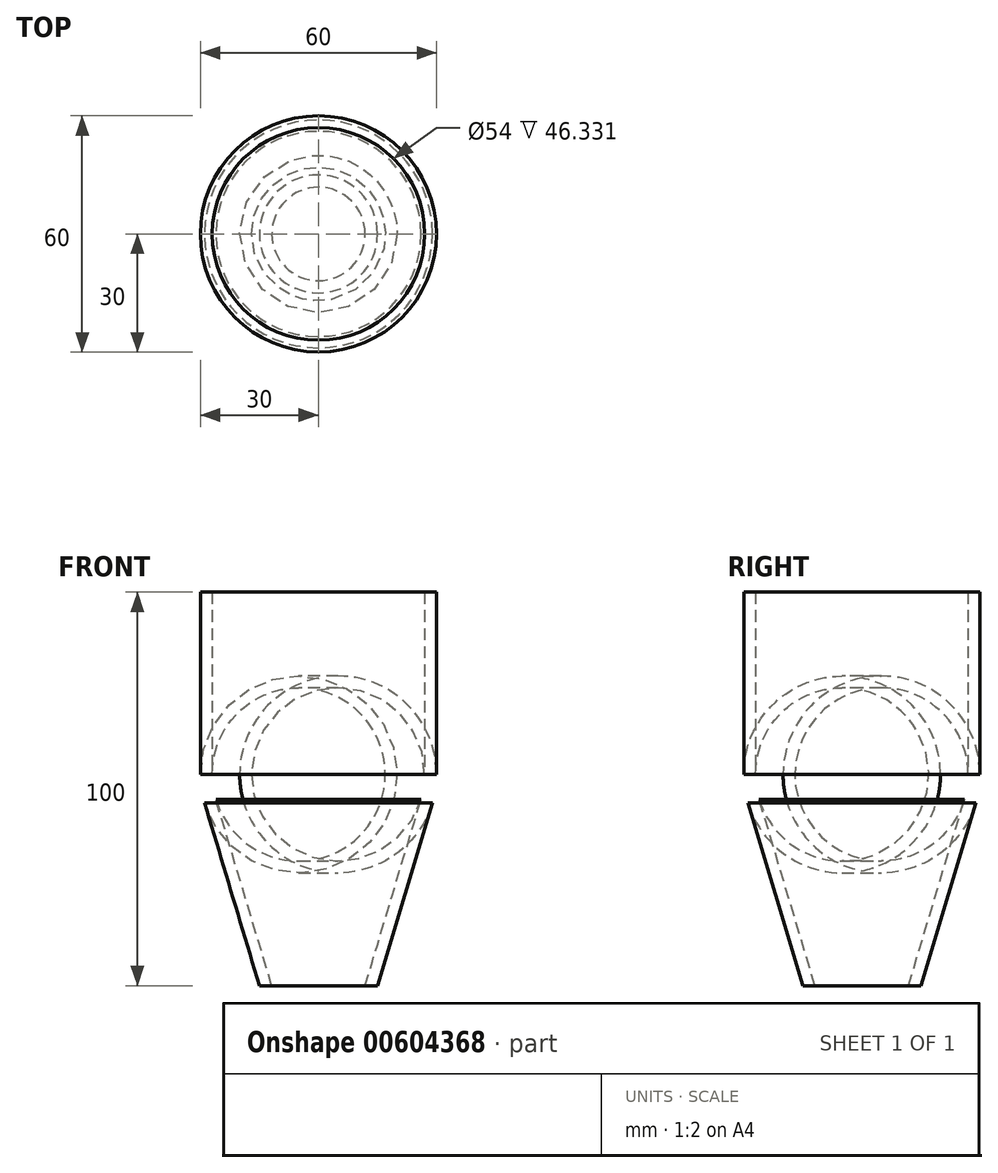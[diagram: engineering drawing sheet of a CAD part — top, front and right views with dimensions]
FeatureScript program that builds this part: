
annotation { "Feature Type Name" : "Feature", "Feature Type Description" : "" }
export const myFeature = defineFeature(function(context is Context, id is Id, definition is map)
    precondition{}
    {
        {
            var Q0;
            Q0=qCreatedBy(makeId("Front.planeOp"),FACE);
            var sketch = newSketch(context, id + "F0", { "sketchPlane" : qUnion([Q0])});
            skLineSegment(sketch, "E0", {"start": v(0, 0) * mm, "end": v(0, 100) * mm});
            skLineSegment(sketch, "E1", {"start": v(0, 100) * mm, "end": v(30, 100) * mm});
            skLineSegment(sketch, "E2", {"start": v(30, 100) * mm, "end": v(30, 50) * mm});
            skLineSegment(sketch, "E3", {"start": v(30, 50) * mm, "end": v(15, 0) * mm});
            skLineSegment(sketch, "E4", {"start": v(15, 0) * mm, "end": v(0, 0) * mm});
            skSolve(sketch);
        }
        {
            var Q0;
            Q0=makeQuery(id+"F0.imprint","IMPRINT",FACE,{"disambiguationData":[TD([[makeQuery(id+"F0.imprint","IMPRINT",EDGE,{"derivedFrom":sQuery(id+"F0.wireOp",EDGE,"E0")}),-1.0]])]});
            var Q1;
            Q1=sQuery(id+"F0.wireOp",EDGE,"E0");
            revolve(context, id + "F1", {"entities" : qUnion([Q0]), "axis" : qUnion([Q1]), "revolveType" : RevolveType.FULL});
        }
        {
            var Q0;
            Q0=makeQuery(id+"F1.opRevolve","SWEPT_EDGE",EDGE,{"disambiguationData":[OSD([sQuery(id+"F0.wireOp",EDGE,"E2"),sQuery(id+"F0.wireOp",EDGE,"E3")])]});
            fillet(context, id + "F2", {"entities" : qUnion([Q0]), "radius" : 25 * mm, "tangentPropagation" : true, "allowEdgeOverflow" : false});
        }
        {
            var Q0;
            Q0=makeQuery(id+"F1.opRevolve","SWEPT_FACE",FACE,{"disambiguationData":[OSD([sQuery(id+"F0.wireOp",EDGE,"E1")])]});
            var Q1;
            Q1=makeQuery(id+"F1.opRevolve","SWEPT_FACE",FACE,{"disambiguationData":[OSD([sQuery(id+"F0.wireOp",EDGE,"E4")])]});
            shell(context, id + "F3", {"entities" : qUnion([Q0, Q1]), "thickness" : 3 * mm});
        }
    });
